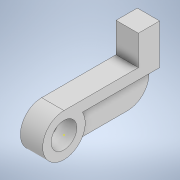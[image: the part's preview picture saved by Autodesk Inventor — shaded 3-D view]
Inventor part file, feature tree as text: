
AUTODESK INVENTOR PART (.ipt)
format: ipt  version: 2020 (Build 240168000, 168)  size: 152,064 bytes
history: native  units: in
note: dims shown in document units (in); Inventor stores cm internally (conversion verified against a paired STEP export)
features: sketch x5, extrude x4, fillet x1, chamfer x1
ambient origin geometry x8: Origin, YZ Plane, XZ Plane, XY Plane, X Axis, Y Axis, Z Axis, Center Point
bodies: Solid1 (feature_tree)
feature tree (11):
  extrude  "Extrusion1"  Depth=0.2in
  extrude  "Extrusion2"  Depth=0.2in
  fillet  "Fillet1"  Radius=0.9in
  sketch  "Sketch3"  dims[d5=0.2in d6=0.28in d7=0.21in d8=0.0in]
  extrude  "Extrusion3"  Depth=0.28in
  chamfer  "Chamfer1"  Distance=0.21in
  extrude  "Extrusion5"  Depth=0.21in TaperAngle=0.0deg
  sketch  "Sketch1"  dims[d0=0.242in d1=0.2in]
  sketch  "Sketch2"  dims[d2=0.2in d3=0.2in d4=0.9in]
  sketch  "Sketch4"  dims[d9=0.125in d10=0.21in d11=0.0in]
  sketch  "Sketch6"  dims[d12=0.2in d13=0.1in d14=0.0in d15=0.1in d16=0.125in d17=45.0deg d30=0.242in d31=0.16in d32=-0.0275in]
